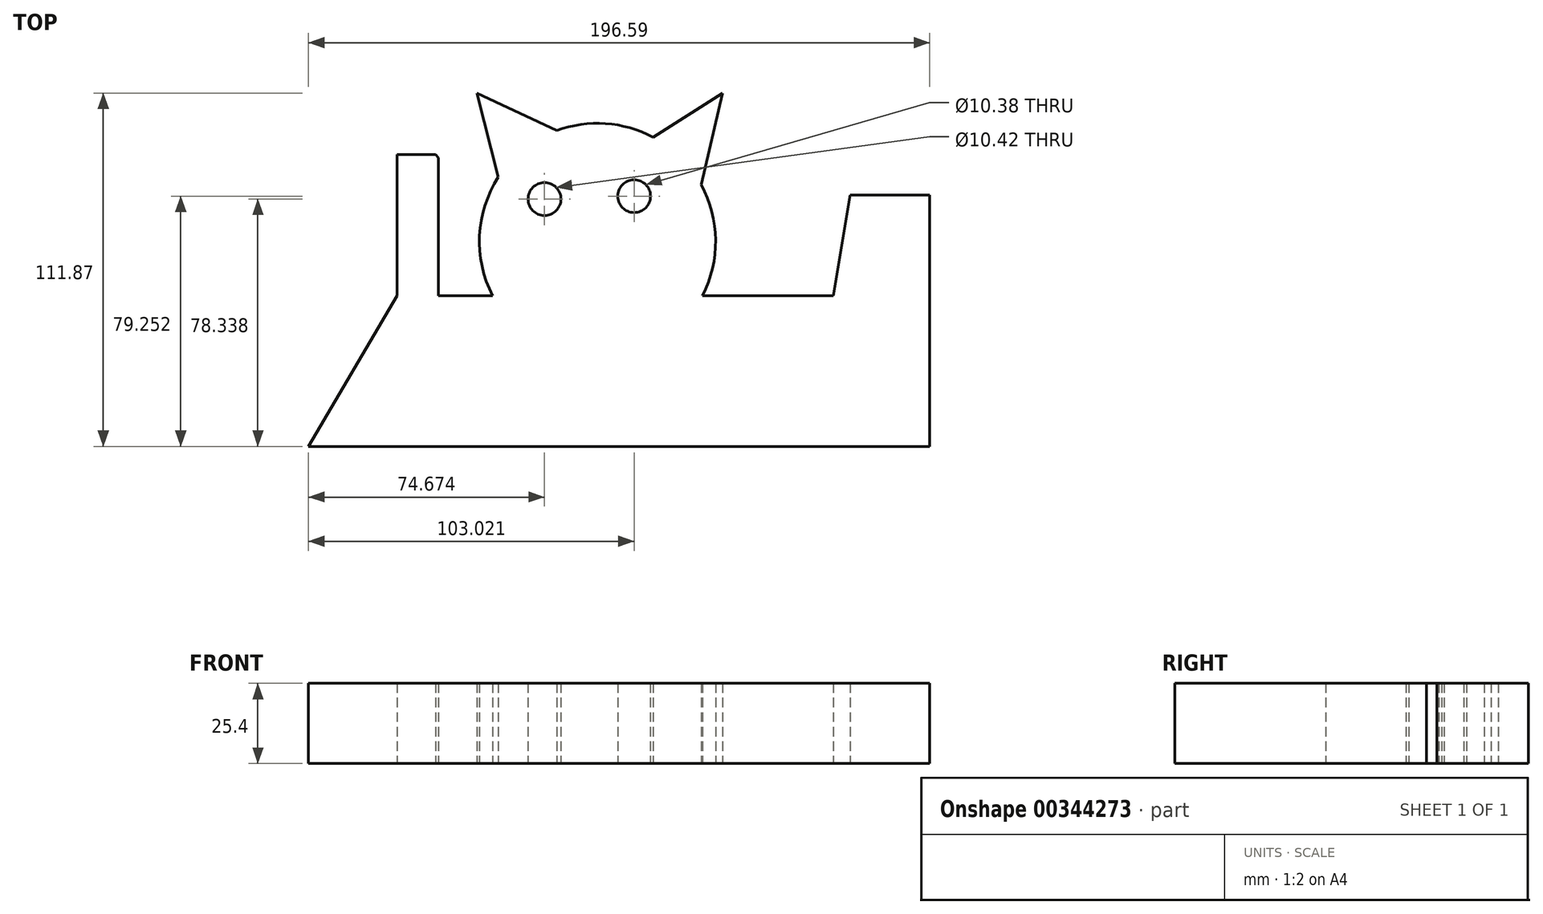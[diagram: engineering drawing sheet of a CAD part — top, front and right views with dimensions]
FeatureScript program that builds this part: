
annotation { "Feature Type Name" : "Feature", "Feature Type Description" : "" }
export const myFeature = defineFeature(function(context is Context, id is Id, definition is map)
    precondition{}
    {
        {
            var Q0;
            Q0=qCreatedBy(makeId("Top.planeOp"),FACE);
            var sketch = newSketch(context, id + "F0", { "sketchPlane" : qUnion([Q0])});
            skArc(sketch, "E0", {"start": v(-74.65, 29.01) * mm, "mid": v(-80.62, 10.5) * mm, "end": v(-76.48, -8.5) * mm});
            skLineSegment(sketch, "E1", {"start": v(-74.65, 29.01) * mm, "end": v(-81.38, 55.63) * mm});
            skLineSegment(sketch, "E2", {"start": v(-81.38, 55.63) * mm, "end": v(-56.22, 43.76) * mm});
            skLineSegment(sketch, "E3", {"start": v(-25.72, 41.69) * mm, "end": v(-3.66, 55.63) * mm});
            skLineSegment(sketch, "E4", {"start": v(-3.66, 55.63) * mm, "end": v(-10.48, 26.62) * mm});
            skLineSegment(sketch, "E5", {"start": v(-76.48, -8.5) * mm, "end": v(-93.57, -8.5) * mm});
            skLineSegment(sketch, "E6", {"start": v(-106.68, -8.5) * mm, "end": v(-134.72, -56.24) * mm});
            skLineSegment(sketch, "E7", {"start": v(-134.72, -56.24) * mm, "end": v(61.87, -56.24) * mm});
            skLineSegment(sketch, "E8", {"start": v(61.87, -56.24) * mm, "end": v(61.87, 23.32) * mm});
            skLineSegment(sketch, "E9", {"start": v(61.87, 23.32) * mm, "end": v(36.88, 23.32) * mm});
            skLineSegment(sketch, "E10", {"start": v(36.88, 24.23) * mm, "end": v(31.4, -8.5) * mm});
            skLineSegment(sketch, "E11", {"start": v(-10.48, -8.5) * mm, "end": v(31.4, -8.5) * mm});
            skCircle(sketch, "E12", {"center": v(-60.05, 22.1) * mm, "radius": 5.2 * mm});
            skCircle(sketch, "E13", {"center": v(-31.7, 23.01) * mm, "radius": 5.2 * mm});
            skLineSegment(sketch, "E14", {"start": v(-106.68, -8.5) * mm, "end": v(-106.68, 36.12) * mm});
            skLineSegment(sketch, "E15", {"start": v(-106.68, 36.12) * mm, "end": v(-94.49, 36.12) * mm});
            skLineSegment(sketch, "E16", {"start": v(-93.57, 35.2) * mm, "end": v(-93.57, -8.5) * mm});
            skArc(sketch, "E17.trimOffspring", {"start": v(-25.72, 41.69) * mm, "mid": v(-40.75, 45.98) * mm, "end": v(-56.22, 43.76) * mm});
            skArc(sketch, "E18.trimOffspring", {"start": v(-10.08, -8.5) * mm, "mid": v(-5.9, 9.12) * mm, "end": v(-10.48, 26.62) * mm});
            skLineSegment(sketch, "E19", {"start": v(-94.49, 36.12) * mm, "end": v(-93.57, 35.2) * mm});
            skLineSegment(sketch, "E20", {"start": v(36.88, 23.32) * mm, "end": v(36.73, 23.32) * mm});
            skLineSegment(sketch, "E21", {"start": v(-108.81, 42.32) * mm, "end": v(-90.22, 42.32) * mm});
            skPoint(sketch, "E21.startSnap0", {"position": v(-78.02, 42.32) * mm});
            skLineSegment(sketch, "E22", {"start": v(-90.22, 42.32) * mm, "end": v(-90.22, -3.5) * mm});
            skLineSegment(sketch, "E23", {"start": v(-90.22, -3.5) * mm, "end": v(-82, -3.5) * mm});
            skFitSpline(sketch, "E24", {"points": [v(-82, -3.5) * mm, v(-85.04, 4.42) * mm, v(-85.65, 14.48) * mm, v(-82, 27.28) * mm, v(-79.55, 31.55) * mm, v(-78.94, 31.55) * mm], "startDerivative": vector(-15.17, 33.7) * mm, "endDerivative": vector(9.44, -2.84) * mm});
            skLineSegment(sketch, "E25", {"start": v(-78.94, 31.55) * mm, "end": v(-88.7, 62.33) * mm});
            skLineSegment(sketch, "E26", {"start": v(-88.7, 62.33) * mm, "end": v(-57.91, 48.62) * mm});
            skFitSpline(sketch, "E27", {"points": [v(-57.91, 48.62) * mm, v(-50.6, 53.19) * mm, v(-37.19, 53.5) * mm, v(-25.6, 48.62) * mm], "startDerivative": vector(22.18, 18.47) * mm, "endDerivative": vector(31.21, -16.77) * mm});
            skLineSegment(sketch, "E28", {"start": v(-25.6, 48.62) * mm, "end": v(0, 61.42) * mm});
            skLineSegment(sketch, "E29", {"start": v(0, 61.42) * mm, "end": v(-5.49, 26.06) * mm});
            skFitSpline(sketch, "E30", {"points": [v(-5.49, 26.06) * mm, v(0, 12.65) * mm, v(-3.05, -3.5) * mm, v(-5.49, -4.72) * mm], "startDerivative": vector(18.62, -29.42) * mm, "endDerivative": vector(-14.29, -1.93) * mm});
            skLineSegment(sketch, "E31", {"start": v(-3.05, -3.5) * mm, "end": v(27.43, -3.5) * mm});
            skLineSegment(sketch, "E32", {"start": v(27.43, -3.5) * mm, "end": v(32.95, 29.4) * mm});
            skLineSegment(sketch, "E33", {"start": v(32.95, 29.4) * mm, "end": v(66.75, 29.4) * mm});
            skLineSegment(sketch, "E34", {"start": v(66.75, 29.4) * mm, "end": v(69.5, -62.03) * mm});
            skLineSegment(sketch, "E35", {"start": v(69.5, -62.03) * mm, "end": v(-137.46, -62.03) * mm});
            skLineSegment(sketch, "E36", {"start": v(-137.46, -62.03) * mm, "end": v(-144.48, -60.85) * mm});
            skLineSegment(sketch, "E37", {"start": v(-144.48, -60.85) * mm, "end": v(-113.08, -7.47) * mm});
            skLineSegment(sketch, "E38", {"start": v(-113.08, -6.55) * mm, "end": v(-108.81, 42.32) * mm});
            skSolve(sketch);
        }
        {
            var Q0;
            Q0 = qSketchRegion(id + "F0", true);
            extrude(context, id + "F1", {"entities" : qUnion([Q0]), "depth" : 25.4 * mm});
        }
    });
